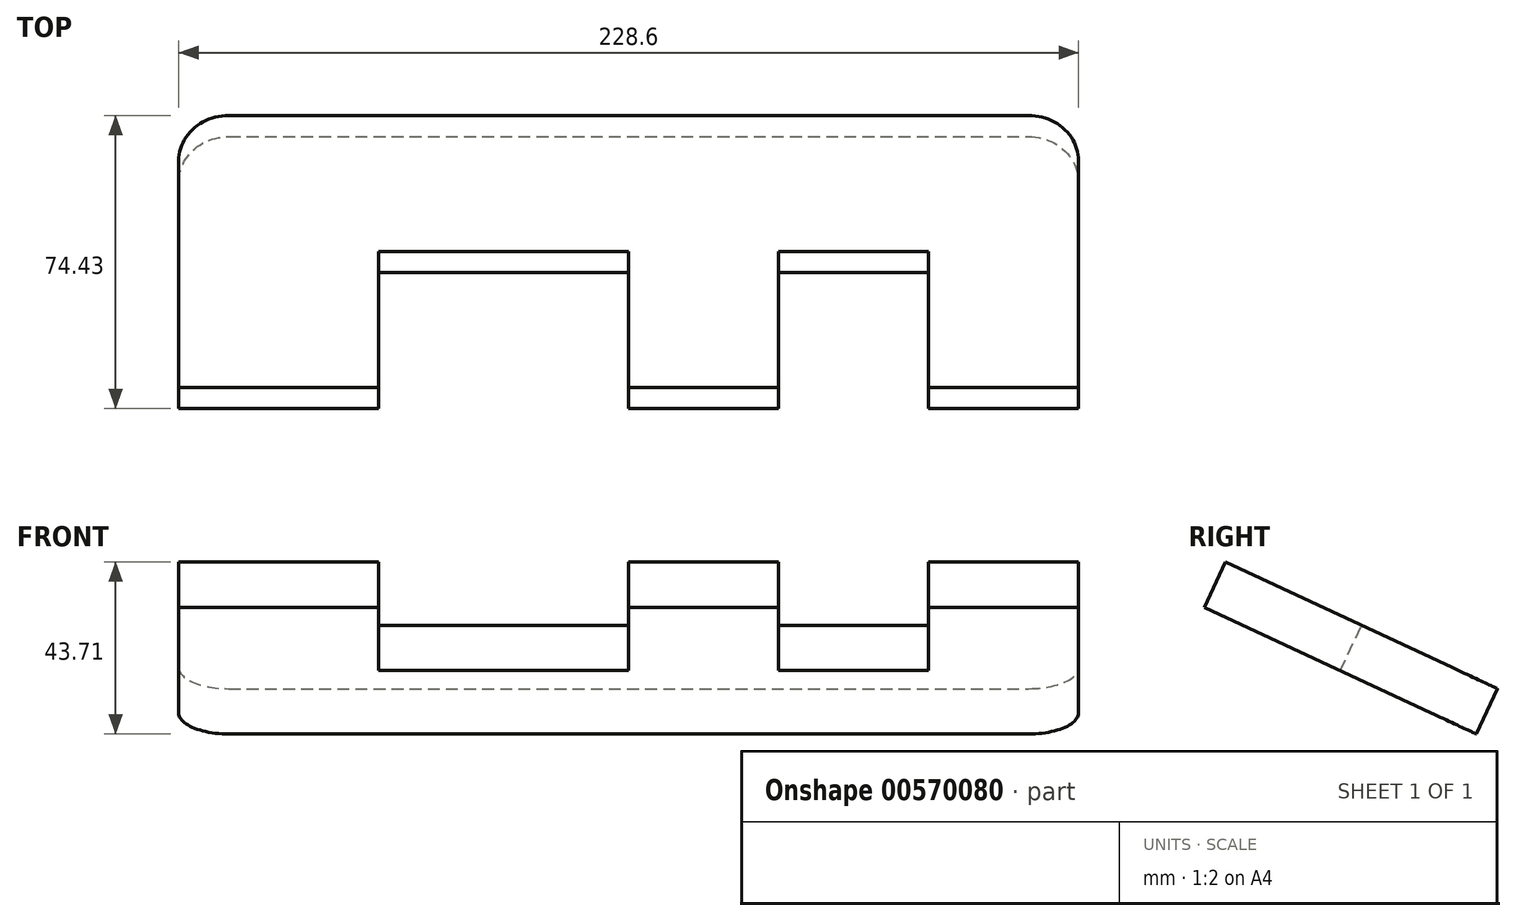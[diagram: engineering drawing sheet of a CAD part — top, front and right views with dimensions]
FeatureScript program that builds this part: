
annotation { "Feature Type Name" : "Feature", "Feature Type Description" : "" }
export const myFeature = defineFeature(function(context is Context, id is Id, definition is map)
    precondition{}
    {
        {
            var Q0;
            Q0=qCreatedBy(makeId("Front.planeOp"),FACE);
            var sketch = newSketch(context, id + "F0", { "sketchPlane" : qUnion([Q0])});
            skLineSegment(sketch, "E0", {"start": v(12.7, 0) * mm, "end": v(215.9, 0) * mm});
            skLineSegment(sketch, "E1", {"start": v(228.6, 12.7) * mm, "end": v(228.6, 76.2) * mm});
            skLineSegment(sketch, "E2", {"start": v(228.6, 76.2) * mm, "end": v(0, 76.2) * mm});
            skLineSegment(sketch, "E3", {"start": v(0, 76.2) * mm, "end": v(0, 12.7) * mm});
            skPoint(sketch, "E4.visualSharp", {"position": v(0, 0) * mm});
            skArc(sketch, "E4.filletArc", {"start": v(0, 12.7) * mm, "mid": v(3.72, 3.72) * mm, "end": v(12.7, 0) * mm});
            skPoint(sketch, "E5.visualSharp", {"position": v(228.6, 0) * mm});
            skArc(sketch, "E5.filletArc", {"start": v(215.9, 0) * mm, "mid": v(224.88, 3.72) * mm, "end": v(228.6, 12.7) * mm});
            skLineSegment(sketch, "E6", {"start": v(228.6, 76.2) * mm, "end": v(190.5, 76.2) * mm});
            skLineSegment(sketch, "E7", {"start": v(0, 76.2) * mm, "end": v(50.8, 76.2) * mm});
            skLineSegment(sketch, "E8", {"start": v(190.5, 76.2) * mm, "end": v(190.5, 38.1) * mm});
            skLineSegment(sketch, "E9", {"start": v(190.5, 38.1) * mm, "end": v(152.4, 38.1) * mm});
            skLineSegment(sketch, "E10", {"start": v(152.4, 38.1) * mm, "end": v(152.4, 76.2) * mm});
            skLineSegment(sketch, "E11", {"start": v(152.4, 76.2) * mm, "end": v(114.3, 76.2) * mm});
            skLineSegment(sketch, "E12", {"start": v(50.8, 76.2) * mm, "end": v(50.8, 38.1) * mm});
            skLineSegment(sketch, "E13", {"start": v(50.8, 38.1) * mm, "end": v(114.3, 38.1) * mm});
            skLineSegment(sketch, "E14", {"start": v(114.3, 76.2) * mm, "end": v(114.3, 38.1) * mm});
            skSolve(sketch);
        }
        {
            var Q0;
            Q0 = qSketchRegion(id + "F0", true);
            extrude(context, id + "F1", {"entities" : qUnion([Q0]), "depth" : 12.7 * mm, "offsetDistance" : 25.4 * mm});
        }
        {
            var Q0;
            {var subQ0=sQuery(id+"F0.wireOp",EDGE,"E12");Q0=makeQuery(id+"F0.imprint","IMPRINT",FACE,{"disambiguationData":[TD([[makeQuery(id+"F0.imprint","IMPRINT",EDGE,{"derivedFrom":subQ0}),1.0]])]});}
            var Q1;
            {var subQ0=sQuery(id+"F0.wireOp",EDGE,"E8");Q1=makeQuery(id+"F0.imprint","IMPRINT",FACE,{"disambiguationData":[TD([[makeQuery(id+"F0.imprint","IMPRINT",EDGE,{"derivedFrom":subQ0}),-1.0]])]});}
            extrude(context, id + "F2", {"entities" : qUnion([Q0, Q1]), "operationType" : NewBodyOperationType.REMOVE, "depth" : 12.7 * mm, "offsetDistance" : 25.4 * mm});
        }
        {
            var Q0;
            Q0=makeQuery(id+"F1.opExtrude","SWEPT_BODY",BODY,{"disambiguationData":[OSD([sQuery(id+"F0.wireOp",EDGE,"E0"),sQuery(id+"F0.wireOp",EDGE,"E1"),sQuery(id+"F0.wireOp",EDGE,"E2"),sQuery(id+"F0.wireOp",EDGE,"E3"),sQuery(id+"F0.wireOp",EDGE,"E4.filletArc"),sQuery(id+"F0.wireOp",EDGE,"E5.filletArc"),sQuery(id+"F0.wireOp",EDGE,"E6"),sQuery(id+"F0.wireOp",EDGE,"E7"),sQuery(id+"F0.wireOp",EDGE,"E11")])]});
            var Q1;
            {var subQ0=sQuery(id+"F0.wireOp",EDGE,"E11");var subQ1=sQuery(id+"F0.wireOp",EDGE,"E7");var subQ2=sQuery(id+"F0.wireOp",EDGE,"E6");var subQ3=sQuery(id+"F0.wireOp",EDGE,"E3");var subQ4=sQuery(id+"F0.wireOp",EDGE,"E2");Q1=makeQuery(id+"F2.boolean.opBoolean","SPLIT",EDGE,{"disambiguationData":[TD([makeQuery(id+"F1.opExtrude","SWEPT_FACE",FACE,{"disambiguationData":[OSD([subQ3])]})])],"derivedFrom":makeQuery(id+"F1.opExtrude","CAP_EDGE",EDGE,{"disambiguationData":[OSD([subQ4,subQ2,subQ1,subQ0])],"isStart":false})});}
            var Q2;
            {var subQ0=sQuery(id+"F0.wireOp",EDGE,"E11");var subQ1=sQuery(id+"F0.wireOp",EDGE,"E7");var subQ2=sQuery(id+"F0.wireOp",EDGE,"E6");var subQ3=sQuery(id+"F0.wireOp",EDGE,"E3");var subQ4=sQuery(id+"F0.wireOp",EDGE,"E2");Q2=makeQuery(id+"F2.boolean.opBoolean","SPLIT",EDGE,{"disambiguationData":[TD([makeQuery(id+"F1.opExtrude","SWEPT_FACE",FACE,{"disambiguationData":[OSD([subQ3])]})])],"derivedFrom":makeQuery(id+"F1.opExtrude","CAP_EDGE",EDGE,{"disambiguationData":[OSD([subQ4,subQ2,subQ1,subQ0])],"isStart":false})});}
            transform(context, id + "F3", {"entities" : qUnion([Q0]), "transformType" : TransformType.ROTATION, "transformAxis" : qUnion([Q2]), "angle" : 295 * degree, "makeCopy" : false});
        }
    });
